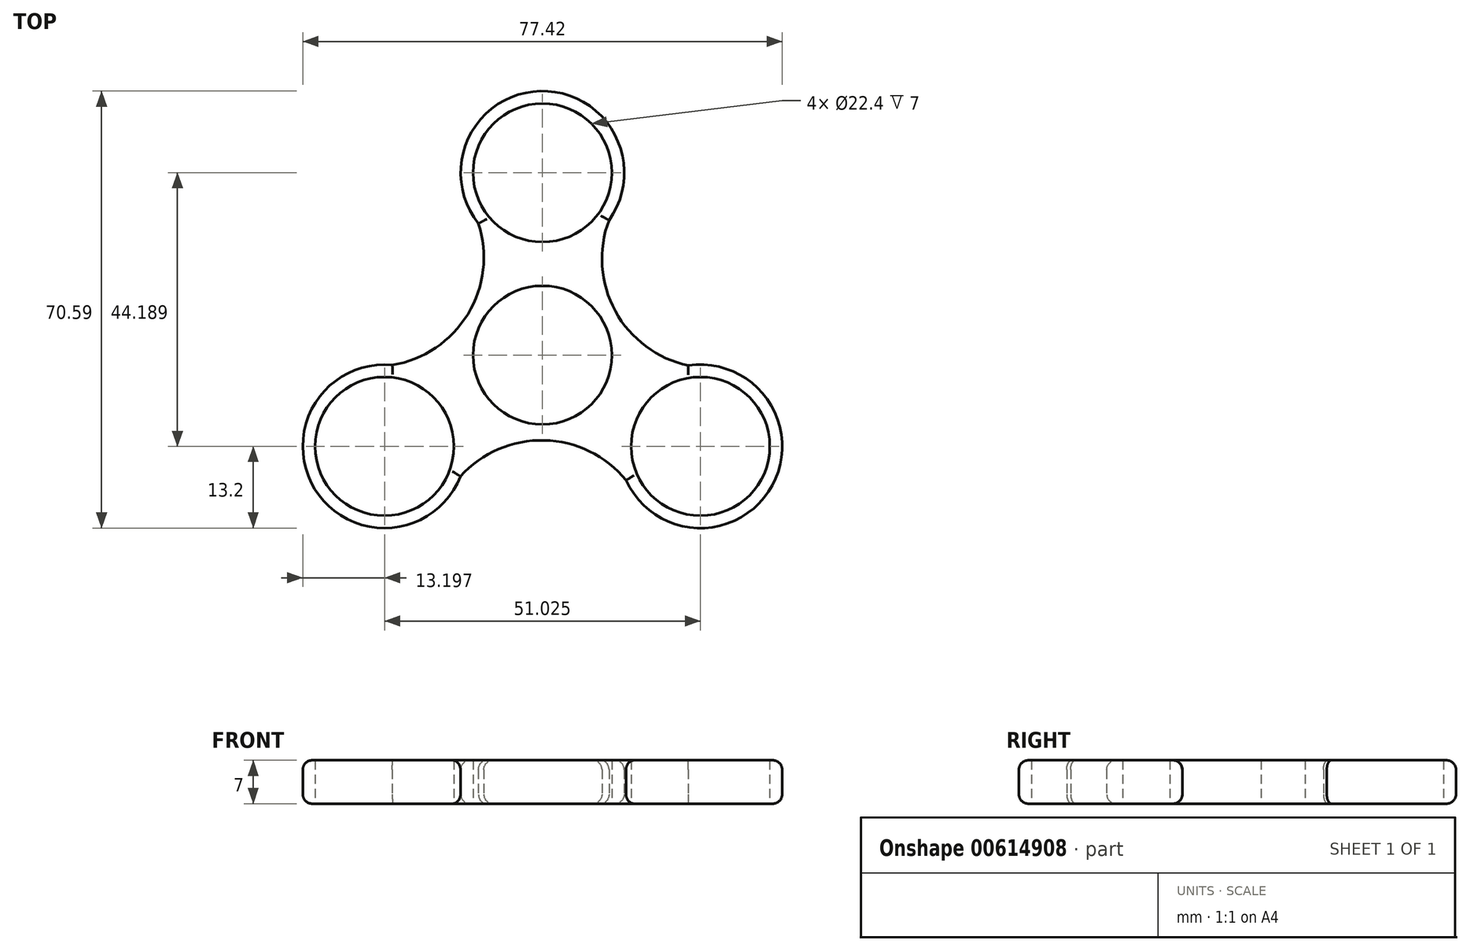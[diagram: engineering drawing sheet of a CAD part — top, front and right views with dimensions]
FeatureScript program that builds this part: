
annotation { "Feature Type Name" : "Feature", "Feature Type Description" : "" }
export const myFeature = defineFeature(function(context is Context, id is Id, definition is map)
    precondition{}
    {
        {
            var Q0;
            Q0=qCreatedBy(makeId("Top.planeOp"),FACE);
            var sketch = newSketch(context, id + "F0", { "sketchPlane" : qUnion([Q0])});
            skCircle(sketch, "E0", {"center": v(0, 0) * mm, "radius": 11.2 * mm});
            skArc(sketch, "E1", {"start": v(10.75, 21.8) * mm, "mid": v(-0.34, 42.65) * mm, "end": v(-10.34, 21.25) * mm});
            skCircle(sketch, "E2", {"center": v(0, 29.46) * mm, "radius": 11.2 * mm});
            skArc(sketch, "E3.1.0", {"start": v(-24.25, -1.6) * mm, "mid": v(-36.77, -21.62) * mm, "end": v(-13.23, -19.58) * mm});
            skCircle(sketch, "E3.1.1", {"center": v(-25.51, -14.73) * mm, "radius": 11.2 * mm});
            skArc(sketch, "E3.2.0", {"start": v(13.5, -20.2) * mm, "mid": v(37.11, -21.03) * mm, "end": v(23.57, -1.67) * mm});
            skCircle(sketch, "E3.2.1", {"center": v(25.51, -14.73) * mm, "radius": 11.2 * mm});
            skArc(sketch, "E4", {"start": v(10.75, 21.8) * mm, "mid": v(11.77, 7.12) * mm, "end": v(23.57, -1.67) * mm});
            skArc(sketch, "E5.1.0", {"start": v(-24.25, -1.6) * mm, "mid": v(-12.05, 6.63) * mm, "end": v(-10.34, 21.25) * mm});
            skArc(sketch, "E5.2.0", {"start": v(13.5, -20.2) * mm, "mid": v(0.28, -13.75) * mm, "end": v(-13.23, -19.58) * mm});
            skSolve(sketch);
        }
        {
            var Q0;
            Q0=makeQuery(id+"F0.imprint","IMPRINT",FACE,{"disambiguationData":[TD([[makeQuery(id+"F0.imprint","IMPRINT",EDGE,{"derivedFrom":sQuery(id+"F0.wireOp",EDGE,"E0")}),-1.0]])]});
            extrude(context, id + "F1", {"entities" : qUnion([Q0]), "depth" : 7 * mm, "offsetDistance" : 25 * mm});
        }
        {
            var Q0;
            Q0=makeQuery(id+"F1.opExtrude","CAP_EDGE",EDGE,{"disambiguationData":[OSD([sQuery(id+"F0.wireOp",EDGE,"E3.1.0")])],"isStart":false});
            var Q1;
            Q1=makeQuery(id+"F1.opExtrude","CAP_EDGE",EDGE,{"disambiguationData":[OSD([sQuery(id+"F0.wireOp",EDGE,"E5.1.0")])],"isStart":false});
            var Q2;
            Q2=makeQuery(id+"F1.opExtrude","CAP_EDGE",EDGE,{"disambiguationData":[OSD([sQuery(id+"F0.wireOp",EDGE,"E1")])],"isStart":false});
            var Q3;
            Q3=makeQuery(id+"F1.opExtrude","CAP_EDGE",EDGE,{"disambiguationData":[OSD([sQuery(id+"F0.wireOp",EDGE,"E4")])],"isStart":false});
            var Q4;
            Q4=makeQuery(id+"F1.opExtrude","CAP_EDGE",EDGE,{"disambiguationData":[OSD([sQuery(id+"F0.wireOp",EDGE,"E3.2.0")])],"isStart":false});
            var Q5;
            Q5=makeQuery(id+"F1.opExtrude","CAP_EDGE",EDGE,{"disambiguationData":[OSD([sQuery(id+"F0.wireOp",EDGE,"E5.2.0")])],"isStart":false});
            fillet(context, id + "F2", {"entities" : qUnion([Q0, Q1, Q2, Q3, Q4, Q5]), "radius" : 1.5 * mm, "tangentPropagation" : true, "allowEdgeOverflow" : false});
        }
        {
            var Q0;
            Q0=makeQuery(id+"F1.opExtrude","CAP_EDGE",EDGE,{"disambiguationData":[OSD([sQuery(id+"F0.wireOp",EDGE,"E5.1.0")])],"isStart":true});
            var Q1;
            Q1=makeQuery(id+"F1.opExtrude","CAP_EDGE",EDGE,{"disambiguationData":[OSD([sQuery(id+"F0.wireOp",EDGE,"E1")])],"isStart":true});
            var Q2;
            Q2=makeQuery(id+"F1.opExtrude","CAP_EDGE",EDGE,{"disambiguationData":[OSD([sQuery(id+"F0.wireOp",EDGE,"E4")])],"isStart":true});
            var Q3;
            Q3=makeQuery(id+"F1.opExtrude","CAP_EDGE",EDGE,{"disambiguationData":[OSD([sQuery(id+"F0.wireOp",EDGE,"E3.2.0")])],"isStart":true});
            var Q4;
            Q4=makeQuery(id+"F1.opExtrude","CAP_EDGE",EDGE,{"disambiguationData":[OSD([sQuery(id+"F0.wireOp",EDGE,"E3.1.0")])],"isStart":true});
            var Q5;
            Q5=makeQuery(id+"F1.opExtrude","CAP_EDGE",EDGE,{"disambiguationData":[OSD([sQuery(id+"F0.wireOp",EDGE,"E5.2.0")])],"isStart":true});
            fillet(context, id + "F3", {"entities" : qUnion([Q0, Q1, Q2, Q3, Q4, Q5]), "radius" : 1.5 * mm, "tangentPropagation" : true, "allowEdgeOverflow" : false});
        }
    });
